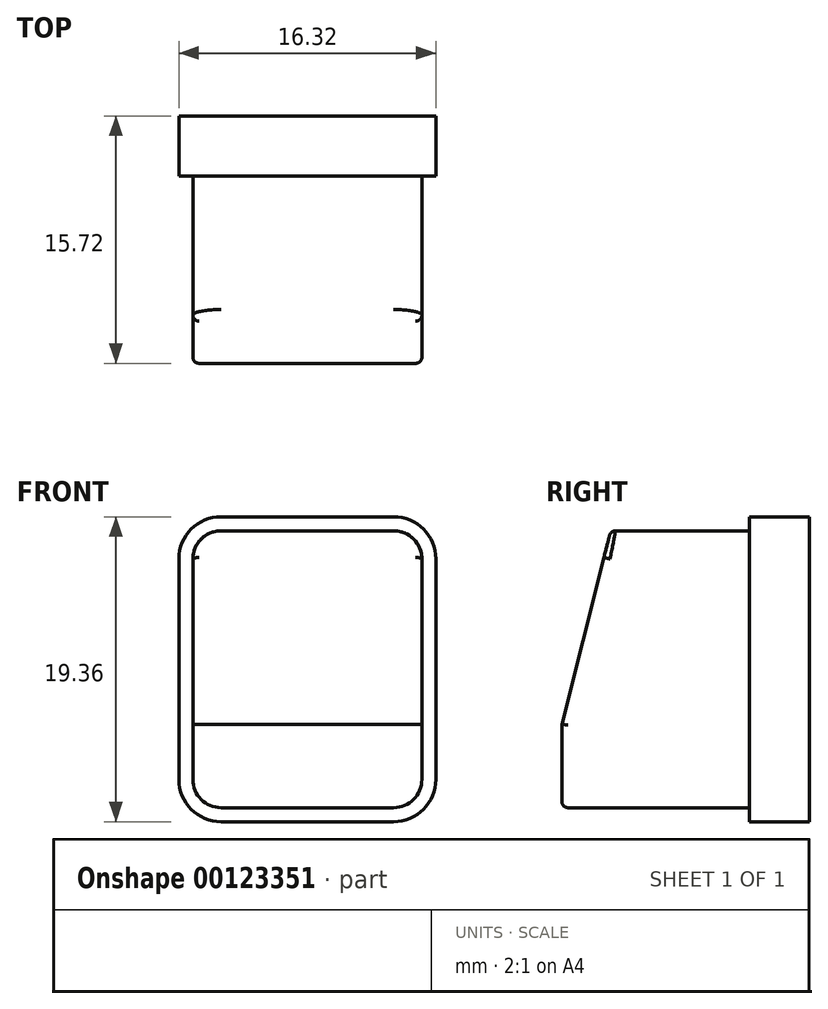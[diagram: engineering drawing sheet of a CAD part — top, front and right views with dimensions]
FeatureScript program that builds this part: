
annotation { "Feature Type Name" : "Feature", "Feature Type Description" : "" }
export const myFeature = defineFeature(function(context is Context, id is Id, definition is map)
    precondition{}
    {
        {
            var Q0;
            Q0=qCreatedBy(makeId("Front.planeOp"),FACE);
            var sketch = newSketch(context, id + "F0", { "sketchPlane" : qUnion([Q0])});
            skArc(sketch, "E0.0", {"start": v(-5.48, 8.8) * mm, "mid": v(-6.75, 8.27) * mm, "end": v(-7.27, 7) * mm});
            skLineSegment(sketch, "E0.1", {"start": v(-5.48, 8.8) * mm, "end": v(5.48, 8.8) * mm});
            skLineSegment(sketch, "E0.2", {"start": v(-7.27, 7) * mm, "end": v(-7.27, -7) * mm});
            skArc(sketch, "E0.3", {"start": v(7.27, 7) * mm, "mid": v(6.75, 8.27) * mm, "end": v(5.48, 8.8) * mm});
            skArc(sketch, "E0.4", {"start": v(-7.27, -7) * mm, "mid": v(-6.75, -8.27) * mm, "end": v(-5.48, -8.8) * mm});
            skLineSegment(sketch, "E0.5", {"start": v(-5.48, -8.8) * mm, "end": v(5.48, -8.8) * mm});
            skArc(sketch, "E0.6", {"start": v(5.48, -8.8) * mm, "mid": v(6.75, -8.27) * mm, "end": v(7.27, -7) * mm});
            skLineSegment(sketch, "E0.7", {"start": v(7.27, 7) * mm, "end": v(7.27, -7) * mm});
            skSolve(sketch);
        }
        {
            var Q0;
            Q0 = qSketchRegion(id + "F0", true);
            extrude(context, id + "F1", {"entities" : qUnion([Q0]), "oppositeDirection" : true, "depth" : 11.9 * mm});
        }
        {
            var Q0;
            Q0=makeQuery(id+"F1.opExtrude","CAP_FACE",FACE,{"disambiguationData":[OSD([sQuery(id+"F0.wireOp",EDGE,"E0.0"),sQuery(id+"F0.wireOp",EDGE,"E0.1"),sQuery(id+"F0.wireOp",EDGE,"E0.2"),sQuery(id+"F0.wireOp",EDGE,"E0.3"),sQuery(id+"F0.wireOp",EDGE,"E0.4"),sQuery(id+"F0.wireOp",EDGE,"E0.5"),sQuery(id+"F0.wireOp",EDGE,"E0.6"),sQuery(id+"F0.wireOp",EDGE,"E0.7")])],"isStart":false});
            var sketch = newSketch(context, id + "F2", { "sketchPlane" : qUnion([Q0])});
            skArc(sketch, "E1.0", {"start": v(5.48, 9.68) * mm, "mid": v(7.38, 8.9) * mm, "end": v(8.16, 7) * mm});
            skLineSegment(sketch, "E1.1", {"start": v(8.16, 7) * mm, "end": v(8.16, -7) * mm});
            skLineSegment(sketch, "E1.2", {"start": v(5.48, 9.68) * mm, "end": v(-5.48, 9.68) * mm});
            skArc(sketch, "E1.3", {"start": v(8.16, -7) * mm, "mid": v(7.38, -8.9) * mm, "end": v(5.48, -9.68) * mm});
            skArc(sketch, "E1.4", {"start": v(-8.16, 7) * mm, "mid": v(-7.38, 8.9) * mm, "end": v(-5.48, 9.68) * mm});
            skLineSegment(sketch, "E1.5", {"start": v(-8.16, 7) * mm, "end": v(-8.16, -7) * mm});
            skArc(sketch, "E1.6", {"start": v(-5.48, -9.68) * mm, "mid": v(-7.38, -8.9) * mm, "end": v(-8.16, -7) * mm});
            skLineSegment(sketch, "E1.7", {"start": v(5.48, -9.68) * mm, "end": v(-5.48, -9.68) * mm});
            skSolve(sketch);
        }
        {
            var Q0;
            Q0 = qSketchRegion(id + "F2", true);
            extrude(context, id + "F3", {"entities" : qUnion([Q0]), "operationType" : NewBodyOperationType.ADD, "depth" : 3.81 * mm});
        }
        {
            var Q0;
            Q0=makeQuery(id+"F1.opExtrude","SWEPT_FACE",FACE,{"disambiguationData":[OSD([sQuery(id+"F0.wireOp",EDGE,"E0.2")])]});
            var sketch = newSketch(context, id + "F4", { "sketchPlane" : qUnion([Q0])});
            skLineSegment(sketch, "E2.0", {"start": v(0, 7) * mm, "end": v(0, -7) * mm});
            skLineSegment(sketch, "E3.0", {"start": v(0, 7) * mm, "end": v(0, 8.8) * mm});
            skLineSegment(sketch, "E4.0", {"start": v(-11.9, 8.8) * mm, "end": v(0, 8.8) * mm});
            skLineSegment(sketch, "E5", {"start": v(0, -3.5) * mm, "end": v(-3.1, 8.8) * mm});
            skLineSegment(sketch, "E6", {"start": v(-3.1, 8.8) * mm, "end": v(0, 8.8) * mm});
            skSolve(sketch);
        }
        {
            var Q0;
            Q0 = qSketchRegion(id + "F4", true);
            var Q1;
            Q1=makeQuery(id+"F1.opExtrude","SWEPT_FACE",FACE,{"disambiguationData":[OSD([sQuery(id+"F0.wireOp",EDGE,"E0.7")])]});
            extrude(context, id + "F5", {"entities" : qUnion([Q0]), "operationType" : NewBodyOperationType.REMOVE, "endBound" : BoundingType.UP_TO_SURFACE, "oppositeDirection" : true, "endBoundEntityFace" : qUnion([Q1]), "depth" : 25 * mm});
        }
        {
            var Q0;
            Q0=makeQuery(id+"F3.opExtrude","CAP_FACE",FACE,{"disambiguationData":[OSD([sQuery(id+"F2.wireOp",EDGE,"E1.0"),sQuery(id+"F2.wireOp",EDGE,"E1.1"),sQuery(id+"F2.wireOp",EDGE,"E1.2"),sQuery(id+"F2.wireOp",EDGE,"E1.3"),sQuery(id+"F2.wireOp",EDGE,"E1.4"),sQuery(id+"F2.wireOp",EDGE,"E1.5"),sQuery(id+"F2.wireOp",EDGE,"E1.6"),sQuery(id+"F2.wireOp",EDGE,"E1.7")])],"isStart":true});
            cPlane(context, id + "F6", {"entities" : qUnion([Q0]), "cplaneType" : CPlaneType.OFFSET, "offset" : 0 * mm, "width" : 150 * mm, "height" : 150 * mm});
        }
        {
            var Q0;
            Q0=makeQuery(id+"F5.boolean.opBoolean","COPY",EDGE,{"derivedFrom":makeQuery(id+"F5.opExtrude","SWEPT_EDGE",EDGE,{"disambiguationData":[OSD([sQuery(id+"F4.wireOp",EDGE,"E5"),sQuery(id+"F4.wireOp",EDGE,"E6")])]})});
            var Q1;
            Q1=makeQuery(id+"F5.boolean.opBoolean","INTERSECT",EDGE,{"derivedFrom":[makeQuery(id+"F1.opExtrude","SWEPT_FACE",FACE,{"disambiguationData":[OSD([sQuery(id+"F0.wireOp",EDGE,"E0.3")])]}),makeQuery(id+"F5.opExtrude","SWEPT_FACE",FACE,{"disambiguationData":[OSD([sQuery(id+"F4.wireOp",EDGE,"E5")])]})]});
            var Q2;
            Q2=makeQuery(id+"F5.boolean.opBoolean","COPY",EDGE,{"derivedFrom":makeQuery(id+"F5.opExtrude","CAP_EDGE",EDGE,{"disambiguationData":[OSD([sQuery(id+"F4.wireOp",EDGE,"E5")])],"isStart":false})});
            var Q3;
            Q3=makeQuery(id+"F1.opExtrude","CAP_EDGE",EDGE,{"disambiguationData":[OSD([sQuery(id+"F0.wireOp",EDGE,"E0.7")])],"isStart":true});
            var Q4;
            Q4=makeQuery(id+"F1.opExtrude","CAP_EDGE",EDGE,{"disambiguationData":[OSD([sQuery(id+"F0.wireOp",EDGE,"E0.6")])],"isStart":true});
            var Q5;
            Q5=makeQuery(id+"F1.opExtrude","CAP_EDGE",EDGE,{"disambiguationData":[OSD([sQuery(id+"F0.wireOp",EDGE,"E0.5")])],"isStart":true});
            var Q6;
            Q6=makeQuery(id+"F1.opExtrude","CAP_EDGE",EDGE,{"disambiguationData":[OSD([sQuery(id+"F0.wireOp",EDGE,"E0.2")])],"isStart":true});
            var Q7;
            Q7=makeQuery(id+"F1.opExtrude","CAP_EDGE",EDGE,{"disambiguationData":[OSD([sQuery(id+"F0.wireOp",EDGE,"E0.4")])],"isStart":true});
            var Q8;
            Q8=makeQuery(id+"F5.boolean.opBoolean","COPY",EDGE,{"derivedFrom":makeQuery(id+"F5.opExtrude","CAP_EDGE",EDGE,{"disambiguationData":[OSD([sQuery(id+"F4.wireOp",EDGE,"E5")])],"isStart":true})});
            var Q9;
            Q9=makeQuery(id+"F5.boolean.opBoolean","INTERSECT",EDGE,{"derivedFrom":[makeQuery(id+"F1.opExtrude","SWEPT_FACE",FACE,{"disambiguationData":[OSD([sQuery(id+"F0.wireOp",EDGE,"E0.0")])]}),makeQuery(id+"F5.opExtrude","SWEPT_FACE",FACE,{"disambiguationData":[OSD([sQuery(id+"F4.wireOp",EDGE,"E5")])]})]});
            fillet(context, id + "F7", {"entities" : qUnion([Q0, Q1, Q2, Q3, Q4, Q5, Q6, Q7, Q8, Q9]), "radius" : 0.4 * mm, "tangentPropagation" : true, "allowEdgeOverflow" : false});
        }
    });
